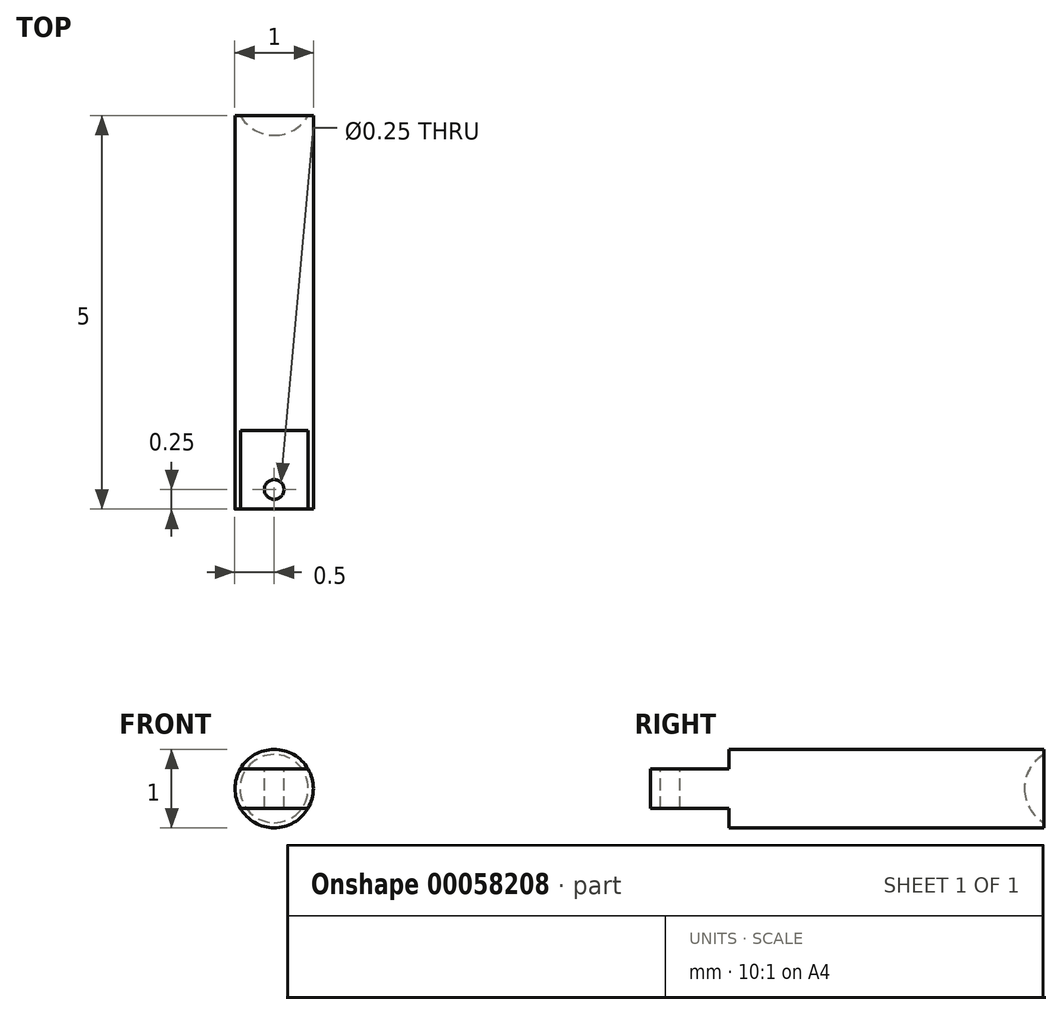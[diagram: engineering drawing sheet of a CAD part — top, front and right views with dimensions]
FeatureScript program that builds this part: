
annotation { "Feature Type Name" : "Feature", "Feature Type Description" : "" }
export const myFeature = defineFeature(function(context is Context, id is Id, definition is map)
    precondition{}
    {
        {
            var Q0;
            Q0=qCreatedBy(makeId("Front.planeOp"),FACE);
            var sketch = newSketch(context, id + "F0", { "sketchPlane" : qUnion([Q0])});
            skCircle(sketch, "E0", {"center": v(0, 0) * mm, "radius": 0.5 * mm});
            skSolve(sketch);
        }
        {
            var Q0;
            Q0=qSketchRegion(id+"F0",true);
            extrude(context, id + "F1", {"entities" : qUnion([Q0]), "endBound" : BoundingType.SYMMETRIC, "depth" : 5 * mm});
        }
        {
            var Q0;
            Q0=qCreatedBy(makeId("Right.planeOp"),FACE);
            var sketch = newSketch(context, id + "F2", { "sketchPlane" : qUnion([Q0])});
            skLineSegment(sketch, "E1.bottom", {"start": v(-2.5, 0.73) * mm, "end": v(-1.5, 0.73) * mm});
            skLineSegment(sketch, "E1.top", {"start": v(-2.5, 0.25) * mm, "end": v(-1.5, 0.25) * mm});
            skLineSegment(sketch, "E1.left", {"start": v(-2.5, 0.73) * mm, "end": v(-2.5, 0.25) * mm});
            skLineSegment(sketch, "E1.right", {"start": v(-1.5, 0.73) * mm, "end": v(-1.5, 0.25) * mm});
            skLineSegment(sketch, "E2.bottom", {"start": v(-2.5, -0.25) * mm, "end": v(-1.5, -0.25) * mm});
            skLineSegment(sketch, "E2.top", {"start": v(-2.5, -0.9) * mm, "end": v(-1.5, -0.9) * mm});
            skLineSegment(sketch, "E2.left", {"start": v(-2.5, -0.25) * mm, "end": v(-2.5, -0.9) * mm});
            skLineSegment(sketch, "E2.right", {"start": v(-1.5, -0.25) * mm, "end": v(-1.5, -0.9) * mm});
            skSolve(sketch);
        }
        {
            var Q0;
            Q0=qSketchRegion(id+"F2",true);
            extrude(context, id + "F3", {"entities" : qUnion([Q0]), "operationType" : NewBodyOperationType.REMOVE, "endBound" : BoundingType.THROUGH_ALL, "oppositeDirection" : true, "depth" : 25 * mm, "hasSecondDirection" : true, "secondDirectionBound" : SecondDirectionBoundingType.THROUGH_ALL, "secondDirectionOppositeDirection" : false, "secondDirectionDepth" : 25 * mm});
        }
        {
            var Q0;
            Q0=qCreatedBy(makeId("Right.planeOp"),FACE);
            var sketch = newSketch(context, id + "F4", { "sketchPlane" : qUnion([Q0])});
            skArc(sketch, "E3", {"start": v(2.5, 0.43) * mm, "mid": v(2.32, 0.25) * mm, "end": v(2.25, 0) * mm});
            skLineSegment(sketch, "E4", {"start": v(2.5, 0.43) * mm, "end": v(2.5, 0) * mm});
            skLineSegment(sketch, "E5", {"start": v(2.5, 0) * mm, "end": v(2.25, 0) * mm});
            skSolve(sketch);
        }
        {
            var Q0;
            Q0=qSketchRegion(id+"F4",true);
            var Q1;
            Q1=sQuery(id+"F4.wireOp",EDGE,"E5");
            revolve(context, id + "F5", {"operationType" : NewBodyOperationType.REMOVE, "entities" : qUnion([Q0]), "axis" : qUnion([Q1]), "revolveType" : RevolveType.FULL, "oppositeDirection" : true});
        }
        {
            var Q0;
            Q0=makeQuery(id+"F3.boolean.opBoolean","COPY",FACE,{"derivedFrom":makeQuery(id+"F3.opExtrude","SWEPT_FACE",FACE,{"disambiguationData":[OSD([sQuery(id+"F2.wireOp",EDGE,"E1.top")])]})});
            var sketch = newSketch(context, id + "F6", { "sketchPlane" : qUnion([Q0])});
            skCircle(sketch, "E6", {"center": v(0, -2.25) * mm, "radius": 0.12 * mm});
            skSolve(sketch);
        }
        {
            var Q0;
            Q0=qSketchRegion(id+"F6",true);
            extrude(context, id + "F7", {"entities" : qUnion([Q0]), "operationType" : NewBodyOperationType.REMOVE, "oppositeDirection" : true, "depth" : 25 * mm});
        }
    });
